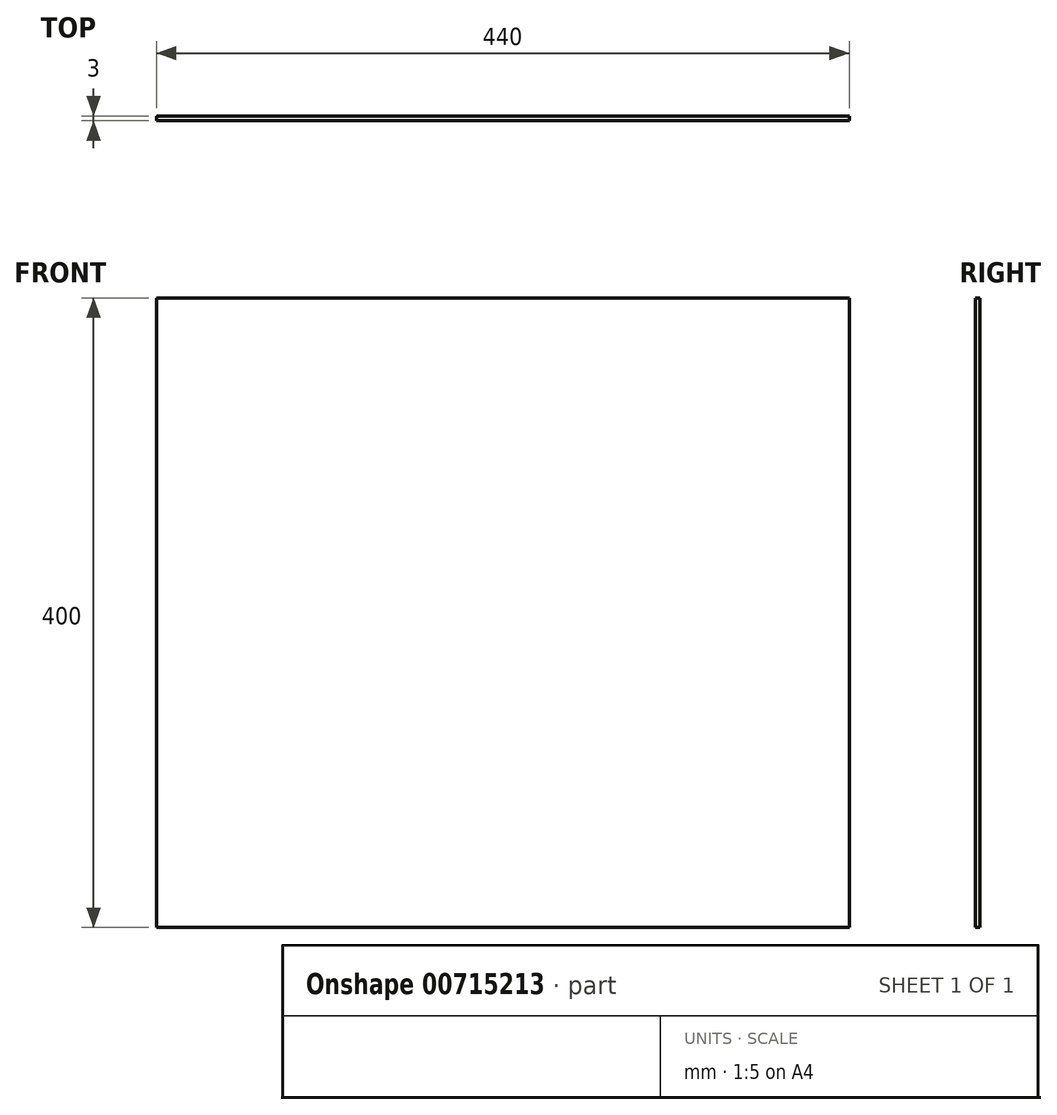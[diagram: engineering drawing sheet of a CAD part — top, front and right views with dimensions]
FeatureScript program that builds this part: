
annotation { "Feature Type Name" : "Feature", "Feature Type Description" : "" }
export const myFeature = defineFeature(function(context is Context, id is Id, definition is map)
    precondition{}
    {
        {
            var Q0;
            Q0=qCreatedBy(makeId("Front.planeOp"),FACE);
            var sketch = newSketch(context, id + "F0", { "sketchPlane" : qUnion([Q0])});
            skLineSegment(sketch, "E0.bottom", {"start": v(220, 200) * mm, "end": v(-220, 200) * mm});
            skLineSegment(sketch, "E0.top", {"start": v(220, -200) * mm, "end": v(-220, -200) * mm});
            skLineSegment(sketch, "E0.left", {"start": v(220, 200) * mm, "end": v(220, -200) * mm});
            skLineSegment(sketch, "E0.right", {"start": v(-220, 200) * mm, "end": v(-220, -200) * mm});
            skPoint(sketch, "E0.middle", {"position": v(0, 0) * mm});
            skSolve(sketch);
        }
        {
            var Q0;
            Q0=makeQuery(id+"F0.imprint","IMPRINT",FACE,{"disambiguationData":[TD([[makeQuery(id+"F0.imprint","IMPRINT",EDGE,{"derivedFrom":sQuery(id+"F0.wireOp",EDGE,"E0.bottom")}),1.0]])]});
            extrude(context, id + "F1", {"entities" : qUnion([Q0]), "depth" : 3 * mm, "offsetDistance" : 25 * mm});
        }
    });
